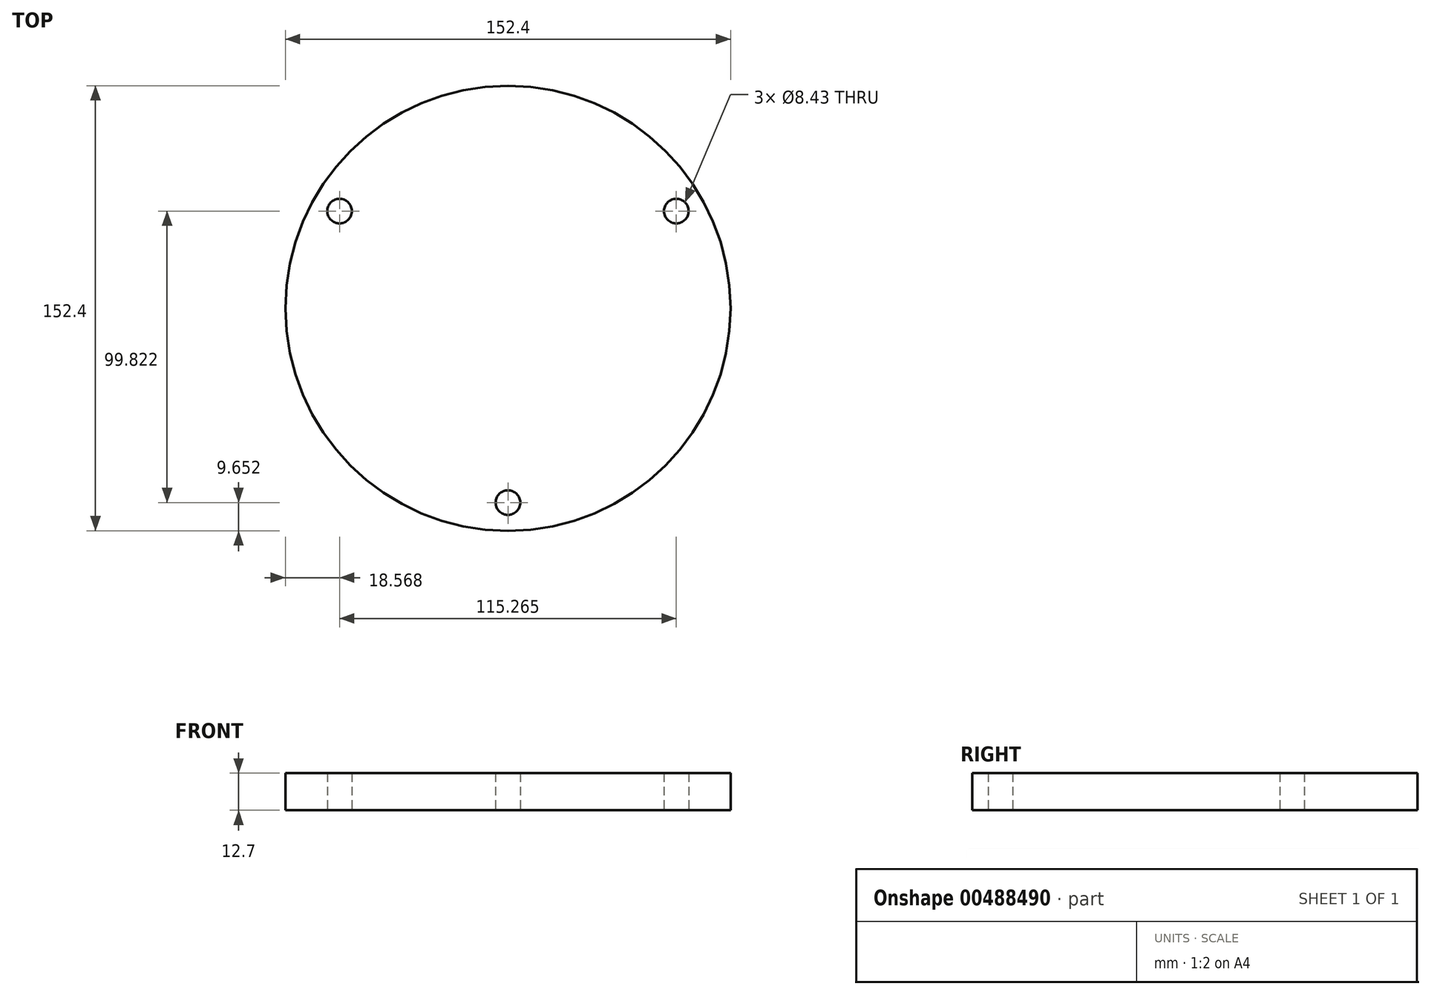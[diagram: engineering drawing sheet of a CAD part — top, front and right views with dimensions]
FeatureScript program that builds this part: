
annotation { "Feature Type Name" : "Feature", "Feature Type Description" : "" }
export const myFeature = defineFeature(function(context is Context, id is Id, definition is map)
    precondition{}
    {
        {
            var Q0;
            Q0=qCreatedBy(makeId("Top.planeOp"),FACE);
            var sketch = newSketch(context, id + "F0", { "sketchPlane" : qUnion([Q0])});
            skCircle(sketch, "E0", {"center": v(0, 0) * mm, "radius": 76.2 * mm});
            skCircle(sketch, "E1", {"center": v(0, 0) * mm, "radius": 66.55 * mm});
            skCircle(sketch, "E2", {"center": v(-57.63, 33.27) * mm, "radius": 4.22 * mm});
            skCircle(sketch, "E3", {"center": v(57.63, 33.27) * mm, "radius": 4.22 * mm});
            skCircle(sketch, "E4", {"center": v(0, -66.55) * mm, "radius": 4.22 * mm});
            skLineSegment(sketch, "E5", {"start": v(0, 0) * mm, "end": v(-57.63, 33.27) * mm});
            skLineSegment(sketch, "E6", {"start": v(0, 0) * mm, "end": v(57.63, 33.27) * mm});
            skLineSegment(sketch, "E7", {"start": v(0, 0) * mm, "end": v(0, -66.55) * mm});
            skSolve(sketch);
        }
        {
            var Q0;
            {var subQ3=sQuery(id+"F0.wireOp",EDGE,"E2");var subQ6=sQuery(id+"F0.wireOp",EDGE,"E1");var subQ9=makeQuery(id+"F0.imprint","INTERSECT",VERTEX,{"disambiguationData":[OD(1.0)],"derivedFrom":[subQ6,subQ3]});Q0=makeQuery(id+"F0.imprint","IMPRINT",FACE,{"disambiguationData":[TD([[makeQuery(id+"F0.imprint","IMPRINT",EDGE,{"disambiguationData":[TD([[subQ9,-1.0]])],"derivedFrom":subQ6}),1.0]])]});}
            var Q1;
            {var subQ5=sQuery(id+"F0.wireOp",EDGE,"E1");var subQ7=sQuery(id+"F0.wireOp",EDGE,"E3");var subQ8=makeQuery(id+"F0.imprint","INTERSECT",VERTEX,{"disambiguationData":[OD(1.0)],"derivedFrom":[subQ5,subQ7]});Q1=makeQuery(id+"F0.imprint","IMPRINT",FACE,{"disambiguationData":[TD([[makeQuery(id+"F0.imprint","IMPRINT",EDGE,{"disambiguationData":[TD([[subQ8,-1.0]])],"derivedFrom":subQ5}),1.0]])]});}
            var Q2;
            Q2=makeQuery(id+"F0.imprint","IMPRINT",FACE,{"disambiguationData":[TD([[makeQuery(id+"F0.imprint","IMPRINT",EDGE,{"derivedFrom":sQuery(id+"F0.wireOp",EDGE,"E0")}),1.0]])]});
            var Q3;
            {var subQ3=sQuery(id+"F0.wireOp",EDGE,"E3");var subQ6=sQuery(id+"F0.wireOp",EDGE,"E1");var subQ9=makeQuery(id+"F0.imprint","INTERSECT",VERTEX,{"disambiguationData":[OD(0.0)],"derivedFrom":[subQ6,subQ3]});Q3=makeQuery(id+"F0.imprint","IMPRINT",FACE,{"disambiguationData":[TD([[makeQuery(id+"F0.imprint","IMPRINT",EDGE,{"disambiguationData":[TD([[subQ9,1.0]])],"derivedFrom":subQ6}),1.0]])]});}
            extrude(context, id + "F1", {"entities" : qUnion([Q0, Q1, Q2, Q3]), "depth" : 12.7 * mm});
        }
    });
